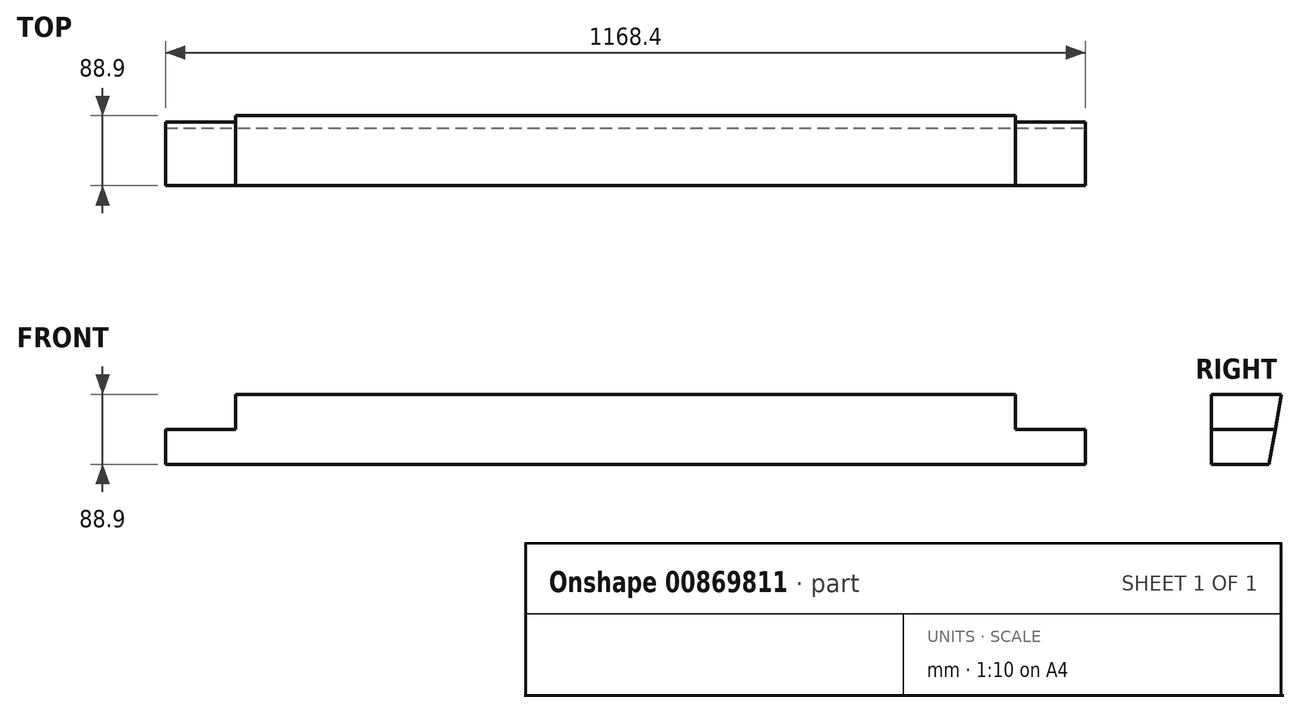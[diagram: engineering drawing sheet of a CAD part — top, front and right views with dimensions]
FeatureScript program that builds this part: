
annotation { "Feature Type Name" : "Feature", "Feature Type Description" : "" }
export const myFeature = defineFeature(function(context is Context, id is Id, definition is map)
    precondition{}
    {
        {
            var Q0;
            Q0=qCreatedBy(makeId("Right.planeOp"),FACE);
            var sketch = newSketch(context, id + "F0", { "sketchPlane" : qUnion([Q0])});
            skLineSegment(sketch, "E0.bottom", {"start": v(-44.45, 44.45) * mm, "end": v(44.45, 44.45) * mm});
            skLineSegment(sketch, "E0.top", {"start": v(-44.45, -44.45) * mm, "end": v(44.45, -44.45) * mm});
            skLineSegment(sketch, "E0.left", {"start": v(-44.45, 44.45) * mm, "end": v(-44.45, -44.45) * mm});
            skLineSegment(sketch, "E0.right", {"start": v(44.45, 44.45) * mm, "end": v(44.45, -44.45) * mm});
            skPoint(sketch, "E0.middle", {"position": v(0, 0) * mm});
            skSolve(sketch);
        }
        {
            var Q0;
            Q0=qSketchRegion(id+"F0",true);
            extrude(context, id + "F1", {"entities" : qUnion([Q0]), "endBound" : BoundingType.SYMMETRIC, "depth" : 1346.2 * mm, "offsetDistance" : 25.4 * mm});
        }
        {
            var Q0;
            Q0=makeQuery(id+"F1.opExtrude","SWEPT_FACE",FACE,{"disambiguationData":[OSD([sQuery(id+"F0.wireOp",EDGE,"E0.left")])]});
            var sketch = newSketch(context, id + "F2", { "sketchPlane" : qUnion([Q0])});
            skLineSegment(sketch, "E1.bottom", {"start": v(-584.2, 44.45) * mm, "end": v(-495.3, 44.45) * mm});
            skLineSegment(sketch, "E1.top", {"start": v(-584.2, 0) * mm, "end": v(-495.3, 0) * mm});
            skLineSegment(sketch, "E1.left", {"start": v(-584.2, 44.45) * mm, "end": v(-584.2, 0) * mm});
            skLineSegment(sketch, "E1.right", {"start": v(-495.3, 44.45) * mm, "end": v(-495.3, 0) * mm});
            skLineSegment(sketch, "E2", {"start": v(0, 44.45) * mm, "end": v(0, -44.45) * mm, "construction": true});
            skLineSegment(sketch, "E3.MirrorCS", {"start": v(584.2, 44.45) * mm, "end": v(495.3, 44.45) * mm});
            skLineSegment(sketch, "E4.MirrorCS", {"start": v(495.3, 44.45) * mm, "end": v(495.3, 0) * mm});
            skLineSegment(sketch, "E5.MirrorCS", {"start": v(584.2, 0) * mm, "end": v(495.3, 0) * mm});
            skLineSegment(sketch, "E6.MirrorCS", {"start": v(584.2, 44.45) * mm, "end": v(584.2, 0) * mm});
            skSolve(sketch);
        }
        {
            var Q0;
            Q0=qSketchRegion(id+"F2",true);
            extrude(context, id + "F3", {"entities" : qUnion([Q0]), "operationType" : NewBodyOperationType.REMOVE, "endBound" : BoundingType.THROUGH_ALL, "oppositeDirection" : true, "depth" : 25.4 * mm, "offsetDistance" : 25.4 * mm});
        }
        {
            var Q0;
            Q0=makeQuery(id+"F1.opExtrude","CAP_FACE",FACE,{"disambiguationData":[OSD([sQuery(id+"F0.wireOp",EDGE,"E0.bottom"),sQuery(id+"F0.wireOp",EDGE,"E0.top"),sQuery(id+"F0.wireOp",EDGE,"E0.left"),sQuery(id+"F0.wireOp",EDGE,"E0.right")])],"isStart":false});
            var sketch = newSketch(context, id + "F4", { "sketchPlane" : qUnion([Q0])});
            skLineSegment(sketch, "E7", {"start": v(44.45, 44.45) * mm, "end": v(28.77, -44.45) * mm});
            skLineSegment(sketch, "E8", {"start": v(28.77, -44.45) * mm, "end": v(44.45, -44.45) * mm});
            skLineSegment(sketch, "E9", {"start": v(44.45, -44.45) * mm, "end": v(44.45, 44.45) * mm});
            skSolve(sketch);
        }
        {
            var Q0;
            Q0 = qSketchRegion(id + "F4", true);
            extrude(context, id + "F5", {"entities" : qUnion([Q0]), "operationType" : NewBodyOperationType.REMOVE, "endBound" : BoundingType.THROUGH_ALL, "oppositeDirection" : true, "depth" : 25.4 * mm, "offsetDistance" : 25.4 * mm});
        }
        {
            var Q0;
            Q0=makeQuery(id+"F1.opExtrude","SWEPT_FACE",FACE,{"disambiguationData":[OSD([sQuery(id+"F0.wireOp",EDGE,"E0.left")])]});
            var sketch = newSketch(context, id + "F6", { "sketchPlane" : qUnion([Q0])});
            skLineSegment(sketch, "E10.bottom", {"start": v(-584.2, 44.45) * mm, "end": v(-673.1, 44.45) * mm});
            skLineSegment(sketch, "E10.top", {"start": v(-584.2, -44.45) * mm, "end": v(-673.1, -44.45) * mm});
            skLineSegment(sketch, "E10.left", {"start": v(-584.2, 44.45) * mm, "end": v(-584.2, -44.45) * mm});
            skLineSegment(sketch, "E10.right", {"start": v(-673.1, 44.45) * mm, "end": v(-673.1, -44.45) * mm});
            skLineSegment(sketch, "E11.bottom", {"start": v(584.2, 44.45) * mm, "end": v(673.1, 44.45) * mm});
            skLineSegment(sketch, "E11.top", {"start": v(584.2, -44.45) * mm, "end": v(673.1, -44.45) * mm});
            skLineSegment(sketch, "E11.left", {"start": v(584.2, 44.45) * mm, "end": v(584.2, -44.45) * mm});
            skLineSegment(sketch, "E11.right", {"start": v(673.1, 44.45) * mm, "end": v(673.1, -44.45) * mm});
            skSolve(sketch);
        }
        {
            var Q0;
            Q0 = qSketchRegion(id + "F6", true);
            extrude(context, id + "F7", {"entities" : qUnion([Q0]), "operationType" : NewBodyOperationType.REMOVE, "endBound" : BoundingType.THROUGH_ALL, "oppositeDirection" : true, "depth" : 25.4 * mm, "offsetDistance" : 25.4 * mm});
        }
    });
